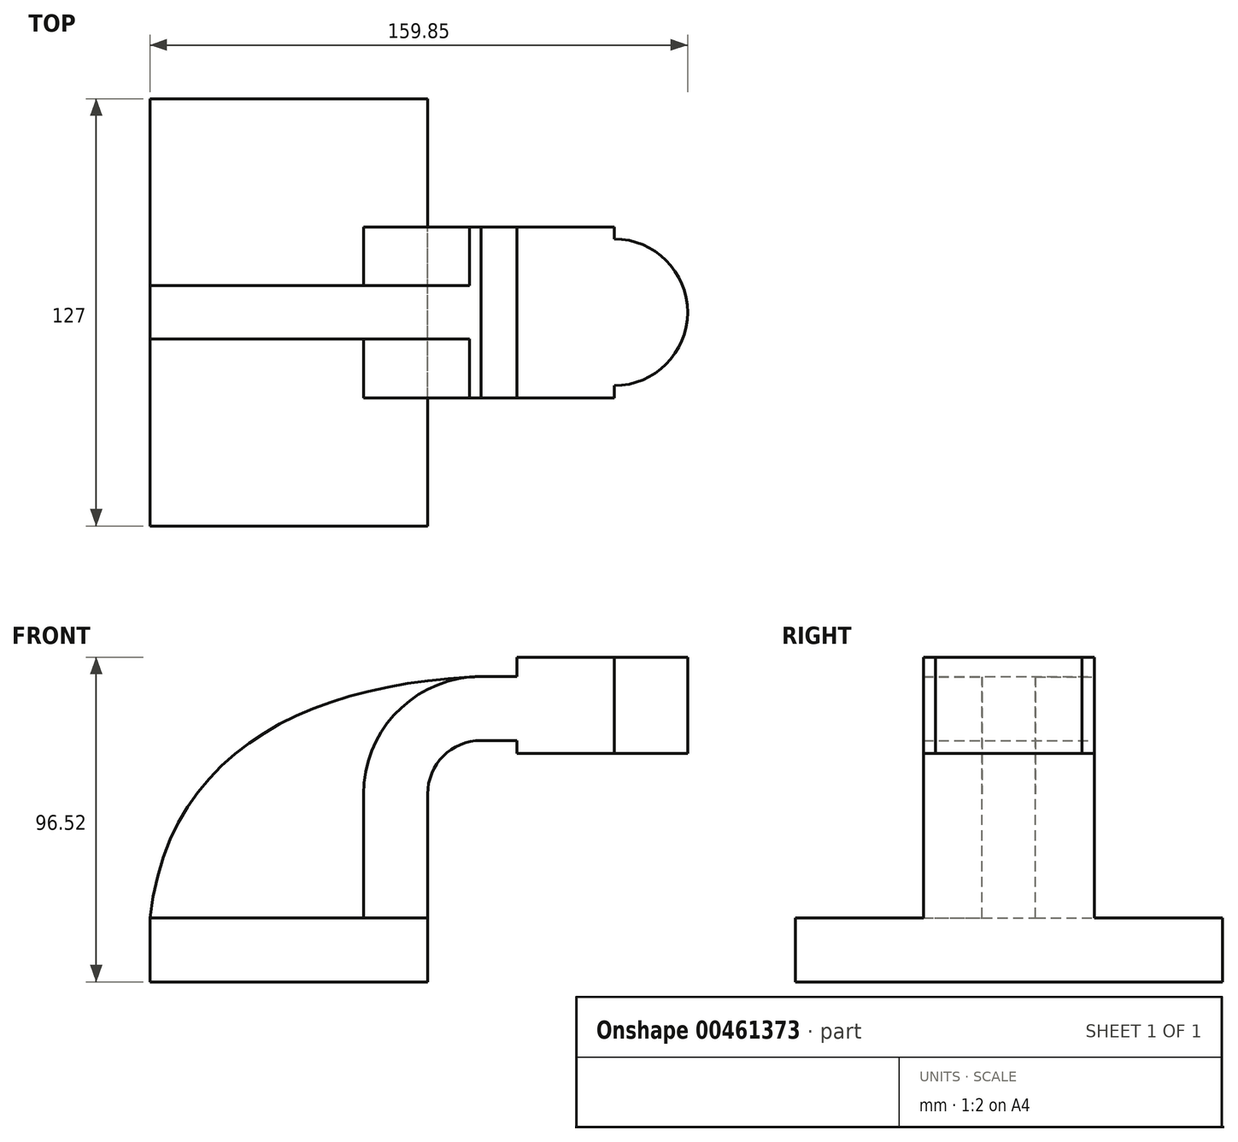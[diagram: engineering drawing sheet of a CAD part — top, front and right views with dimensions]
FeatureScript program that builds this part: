
annotation { "Feature Type Name" : "Feature", "Feature Type Description" : "" }
export const myFeature = defineFeature(function(context is Context, id is Id, definition is map)
    precondition{}
    {
        {
            var Q0;
            Q0=qCreatedBy(makeId("Front.planeOp"),FACE);
            var sketch = newSketch(context, id + "F0", { "sketchPlane" : qUnion([Q0])});
            skLineSegment(sketch, "E0.bottom", {"start": v(-31.82, -20.75) * mm, "end": v(50.73, -20.75) * mm});
            skLineSegment(sketch, "E0.top", {"start": v(-31.82, -39.8) * mm, "end": v(50.73, -39.8) * mm});
            skLineSegment(sketch, "E0.left", {"start": v(-31.82, -20.75) * mm, "end": v(-31.82, -39.8) * mm});
            skLineSegment(sketch, "E0.right", {"start": v(50.73, -20.75) * mm, "end": v(50.73, -39.8) * mm});
            skLineSegment(sketch, "E1", {"start": v(50.73, -20.75) * mm, "end": v(50.73, 16.05) * mm});
            skArc(sketch, "E2", {"start": v(50.73, 16.05) * mm, "mid": v(55.38, 27.28) * mm, "end": v(66.6, 31.93) * mm});
            skLineSegment(sketch, "E3.bottom", {"start": v(77.23, 56.72) * mm, "end": v(128.03, 56.72) * mm});
            skLineSegment(sketch, "E3.top", {"start": v(77.23, 28.14) * mm, "end": v(128.03, 28.14) * mm});
            skLineSegment(sketch, "E3.left", {"start": v(77.23, 56.72) * mm, "end": v(77.23, 28.14) * mm});
            skLineSegment(sketch, "E3.right", {"start": v(128.03, 56.72) * mm, "end": v(128.03, 28.14) * mm});
            skLineSegment(sketch, "E4", {"start": v(66.6, 31.93) * mm, "end": v(102.63, 31.93) * mm});
            skPoint(sketch, "E4.endSnap0", {"position": v(102.63, 28.14) * mm});
            skLineSegment(sketch, "E5.0", {"start": v(66.6, 50.98) * mm, "end": v(104.37, 50.98) * mm});
            skArc(sketch, "E5.1", {"start": v(31.68, 16.05) * mm, "mid": v(41.91, 40.75) * mm, "end": v(66.6, 50.98) * mm});
            skLineSegment(sketch, "E5.2", {"start": v(31.68, -20.75) * mm, "end": v(31.68, 16.05) * mm});
            skLineSegment(sketch, "E6", {"start": v(106.23, 56.72) * mm, "end": v(106.23, 28.14) * mm});
            skFitSpline(sketch, "E7", {"points": [v(-31.82, -20.75) * mm, v(66.6, 50.98) * mm], "startDerivative": vector(17.17, 153.12) * mm, "endDerivative": vector(148.1, 6.16) * mm});
            skSolve(sketch);
        }
        {
            var Q0;
            Q0=makeQuery(id+"F0.imprint","IMPRINT",FACE,{"disambiguationData":[TD([[makeQuery(id+"F0.imprint","IMPRINT",EDGE,{"derivedFrom":sQuery(id+"F0.wireOp",EDGE,"E0.top")}),1.0]])]});
            extrude(context, id + "F1", {"entities" : qUnion([Q0]), "endBound" : BoundingType.SYMMETRIC, "depth" : 127 * mm});
        }
        {
            var Q0;
            {var subQ5=sQuery(id+"F0.wireOp",EDGE,"E1");Q0=makeQuery(id+"F0.imprint","IMPRINT",FACE,{"disambiguationData":[TD([[makeQuery(id+"F0.imprint","IMPRINT",EDGE,{"derivedFrom":subQ5}),1.0]])]});}
            var Q1;
            {var subQ6=sQuery(id+"F0.wireOp",EDGE,"E6");Q1=makeQuery(id+"F0.imprint","IMPRINT",FACE,{"disambiguationData":[TD([[makeQuery(id+"F0.imprint","IMPRINT",EDGE,{"derivedFrom":subQ6}),-1.0]])]});}
            extrude(context, id + "F2", {"entities" : qUnion([Q0, Q1]), "operationType" : NewBodyOperationType.ADD, "endBound" : BoundingType.SYMMETRIC, "depth" : 50.8 * mm});
        }
        {
            var Q0;
            {var subQ3=sQuery(id+"F0.wireOp",EDGE,"E5.2");Q0=makeQuery(id+"F0.imprint","IMPRINT",FACE,{"disambiguationData":[TD([[makeQuery(id+"F0.imprint","IMPRINT",EDGE,{"derivedFrom":subQ3}),1.0]])]});}
            extrude(context, id + "F3", {"entities" : qUnion([Q0]), "operationType" : NewBodyOperationType.ADD, "endBound" : BoundingType.SYMMETRIC, "depth" : 15.88 * mm});
        }
        {
            var Q0;
            {var subQ0=sQuery(id+"F0.wireOp",EDGE,"E3.right");Q0=makeQuery(id+"F0.imprint","IMPRINT",FACE,{"disambiguationData":[TD([[makeQuery(id+"F0.imprint","IMPRINT",EDGE,{"derivedFrom":subQ0}),-1.0]])]});}
            var Q1;
            Q1=sQuery(id+"F0.wireOp",EDGE,"E6");
            revolve(context, id + "F4", {"operationType" : NewBodyOperationType.ADD, "entities" : qUnion([Q0]), "axis" : qUnion([Q1]), "revolveType" : RevolveType.FULL});
        }
    });
